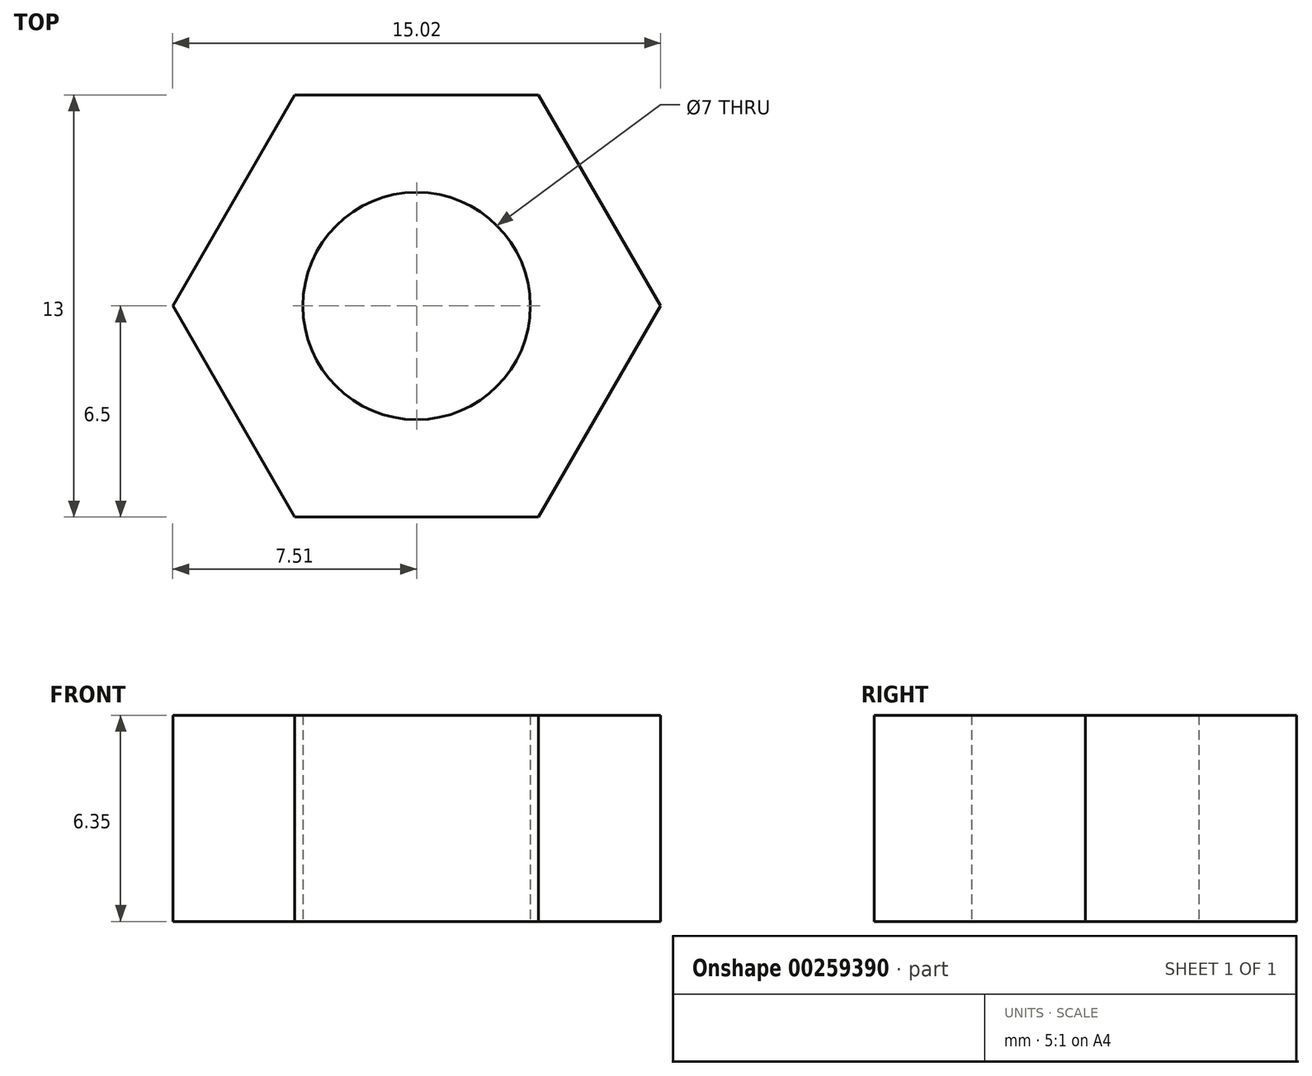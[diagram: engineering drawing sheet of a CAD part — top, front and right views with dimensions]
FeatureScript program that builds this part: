
annotation { "Feature Type Name" : "Feature", "Feature Type Description" : "" }
export const myFeature = defineFeature(function(context is Context, id is Id, definition is map)
    precondition{}
    {
        {
            var Q0;
            Q0=qCreatedBy(makeId("Top.planeOp"),FACE);
            var sketch = newSketch(context, id + "F0", { "sketchPlane" : qUnion([Q0])});
            skCircle(sketch, "E0.cCircle", {"center": v(0, 0) * mm, "radius": 6.5 * mm, "construction": true});
            skLineSegment(sketch, "E0.0", {"start": v(-7.5, 0) * mm, "end": v(-3.75, 6.5) * mm});
            skLineSegment(sketch, "E0.1", {"start": v(-3.75, 6.5) * mm, "end": v(3.75, 6.5) * mm});
            skLineSegment(sketch, "E0.2", {"start": v(3.75, 6.5) * mm, "end": v(7.5, 0) * mm});
            skLineSegment(sketch, "E0.3", {"start": v(7.5, 0) * mm, "end": v(3.75, -6.5) * mm});
            skLineSegment(sketch, "E0.4", {"start": v(3.75, -6.5) * mm, "end": v(-3.75, -6.5) * mm});
            skLineSegment(sketch, "E0.5", {"start": v(-3.75, -6.5) * mm, "end": v(-7.5, 0) * mm});
            skPoint(sketch, "E0.0.midPoint", {"position": v(-5.63, 3.25) * mm});
            skCircle(sketch, "E1", {"center": v(0, 0) * mm, "radius": 3.5 * mm});
            skSolve(sketch);
        }
        {
            var Q0;
            Q0=makeQuery(id+"F0.imprint","IMPRINT",FACE,{"disambiguationData":[TD([[makeQuery(id+"F0.imprint","IMPRINT",EDGE,{"derivedFrom":sQuery(id+"F0.wireOp",EDGE,"E0.0")}),-1.0]])]});
            extrude(context, id + "F1", {"entities" : qUnion([Q0]), "depth" : 6.35 * mm});
        }
    });
